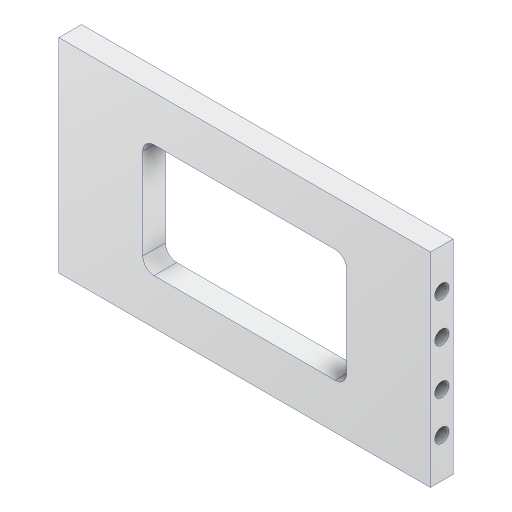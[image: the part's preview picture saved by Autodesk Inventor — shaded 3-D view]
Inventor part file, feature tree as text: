
AUTODESK INVENTOR PART (.ipt)
format: ipt  version: 2023.2 (Build 272271000, 271)  size: 151,040 bytes
history: native  units: mm
features: extrude x3, sketch x3, other x1, mirror x1, fillet x1, projected_geometry x1
ambient origin geometry x8: Origin, YZ Plane, XZ Plane, XY Plane, X Axis, Y Axis, Z Axis, Center Point
bodies: Body1 (feature_tree)
feature tree (10):
  other  "솔리드1"
  extrude  "돌출1"  Depth=65.6mm
  extrude  "돌출2"  Depth=36.0mm
  mirror  "미러1"
  extrude  "돌출3"  Depth=4.0mm TaperAngle=0.0deg
  fillet  "모깎기1"  Radius=2.5mm
  sketch  "스케치1"
  sketch  "스케치2"
  projected_geometry  "투영된 루프1"
  sketch  "스케치3"
